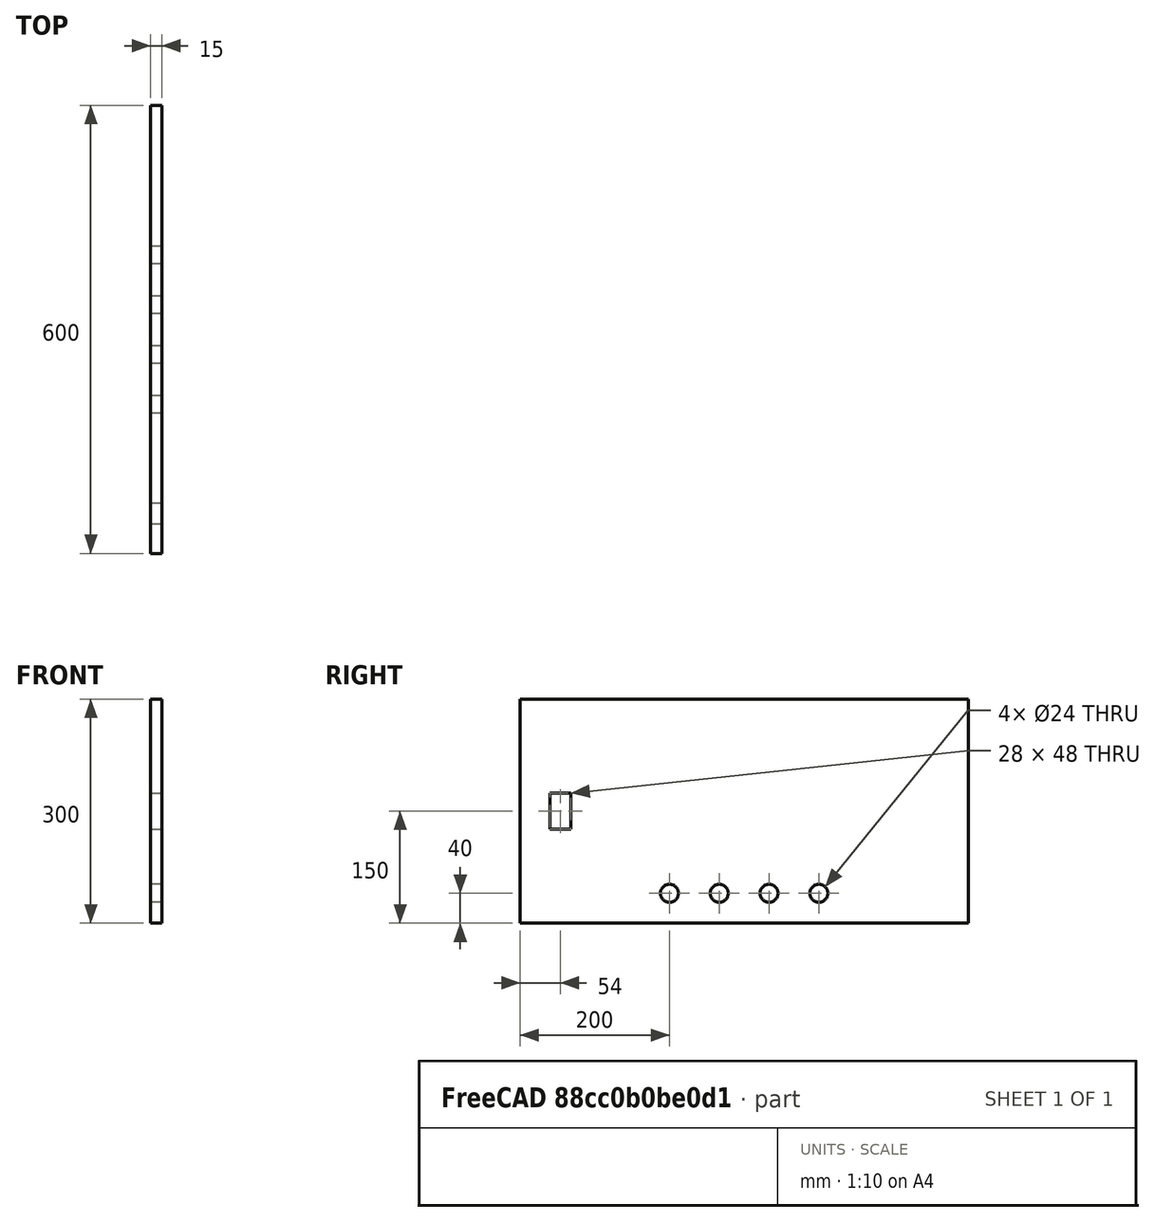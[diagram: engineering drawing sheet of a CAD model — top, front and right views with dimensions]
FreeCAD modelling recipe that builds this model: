
FCSTD DOCUMENT  (FreeCAD 1.0R39319 (Git))
Label: connector_panel
License: All rights reserved
LicenseURL: http://en.wikipedia.org/wiki/All_rights_reserved
objects: Sketcher::SketchObject×1, PartDesign::Pad×1, PartDesign::Body×1
note: 6 computed .brp shape members not serialized (recipe doc carries the construction recipe); baked Part::Feature solids carry a one-line shape summary decoded from their .brp

FEATURE [Sketcher::SketchObject] Sketch  label="connector_panel_sketch"
  ArcFitTolerance = 0
  AttachmentSupport = -> [YZ_Plane]
  FullyConstrained = true
  MakeInternals = false
  MapMode = 5
  Placement = pos=(0,0,0) rot=(0.57735,0.57735,0.57735;2.0944rad)
  sketch-geometry (21):
    g0: LineSegment StartX=0 StartY=0 StartZ=0 EndX=600 EndY=0 EndZ=0
    g1: LineSegment StartX=600 StartY=0 StartZ=0 EndX=600 EndY=300 EndZ=0
    g2: LineSegment StartX=600 StartY=300 StartZ=0 EndX=0 EndY=300 EndZ=0
    g3: LineSegment StartX=0 StartY=300 StartZ=0 EndX=0 EndY=0 EndZ=0
    g4: LineSegment StartX=40 StartY=174 StartZ=0 EndX=68 EndY=174 EndZ=0
    g5: LineSegment StartX=68 StartY=174 StartZ=0 EndX=68 EndY=126 EndZ=0
    g6: LineSegment StartX=68 StartY=126 StartZ=0 EndX=40 EndY=126 EndZ=0
    g7: LineSegment StartX=40 StartY=126 StartZ=0 EndX=40 EndY=174 EndZ=0
    g8: Circle CenterX=200 CenterY=40 CenterZ=0 NormalX=0 NormalY=0 NormalZ=1 AngleXU=0 Radius=12
    g9: Circle CenterX=266.667 CenterY=40 CenterZ=0 NormalX=0 NormalY=0 NormalZ=1 AngleXU=0 Radius=12
    g10: Circle CenterX=333.333 CenterY=40 CenterZ=0 NormalX=0 NormalY=0 NormalZ=1 AngleXU=0 Radius=12
    g11: Circle CenterX=400 CenterY=40 CenterZ=0 NormalX=0 NormalY=0 NormalZ=1 AngleXU=0 Radius=12
    g12: LineSegment [constr] StartX=40 StartY=126 StartZ=0 EndX=0 EndY=126 EndZ=0
    g13: LineSegment [constr] StartX=200 StartY=40 StartZ=0 EndX=266.667 EndY=40 EndZ=0
    g14: LineSegment [constr] StartX=333.333 StartY=40 StartZ=0 EndX=400 EndY=40 EndZ=0
    g15: LineSegment [constr] StartX=40 StartY=126 StartZ=0 EndX=40 EndY=0 EndZ=0
    g16: LineSegment [constr] StartX=40 StartY=174 StartZ=0 EndX=40 EndY=300 EndZ=0
    g17: LineSegment [constr] StartX=200 StartY=40 StartZ=0 EndX=200 EndY=0 EndZ=0
    g18: LineSegment [constr] StartX=266.667 StartY=40 StartZ=0 EndX=333.333 EndY=40 EndZ=0
    g19: LineSegment [constr] StartX=200 StartY=40 StartZ=0 EndX=0 EndY=40 EndZ=0
    g20: LineSegment [constr] StartX=400 StartY=40 StartZ=0 EndX=600 EndY=40 EndZ=0
  constraints (59):
    c: Coincident(g0,g1)
    c: Coincident(g1,g2)
    c: Coincident(g2,g3)
    c: Coincident(g3,g0)
    c: Horizontal(g0)
    c: Horizontal(g2)
    c: Vertical(g1)
    c: Vertical(g3)
    c: Coincident(g0,g-1)
    c: DistanceY(g3,g3) = 300
    c: DistanceX(g0,g0) = 600
    c: Coincident(g4,g5)
    c: Coincident(g5,g6)
    c: Coincident(g6,g7)
    c: Coincident(g7,g4)
    c: Horizontal(g4)
    c: Horizontal(g6)
    c: Vertical(g5)
    c: Vertical(g7)
    c: DistanceX(g4,g4) = 28
    c: DistanceY(g7,g7) = 48
    c: Radius(g8) = 12
    c: Radius(g9) = 12
    c: Radius(g10) = 12
    c: Radius(g11) = 12
    c: Coincident(g12,g6)
    c: PointOnObject(g12,g3)
    c: Horizontal(g12)
    c: Coincident(g13,g8)
    c: Coincident(g13,g9)
    c: Horizontal(g13)
    c: Coincident(g14,g10)
    c: Coincident(g14,g11)
    c: Horizontal(g14)
    c: Equal(g13,g14)
    c: Coincident(g15,g6)
    c: PointOnObject(g15,g0)
    c: Vertical(g15)
    c: Coincident(g16,g4)
    c: PointOnObject(g16,g2)
    c: Vertical(g16)
    c: Equal(g16,g15)
    c: DistanceX(g12,g12) = 40
    c: Coincident(g17,g8)
    c: PointOnObject(g17,g0)
    c: Vertical(g17)
    c: DistanceX(g-1,g17) = 200
    c: Coincident(g18,g9)
    c: Coincident(g18,g10)
    c: Horizontal(g18)
    c: Equal(g18,g14)
    c: DistanceY(g17,g17) = 40
    c: Coincident(g19,g8)
    c: PointOnObject(g19,g3)
    c: Horizontal(g19)
    c: Coincident(g20,g11)
    c: PointOnObject(g20,g1)
    c: Horizontal(g20)
    c: Equal(g19,g20)
FEATURE [PartDesign::Pad] Pad  label="connector_panel_pad"
  AllowMultiFace = false
  Direction = (1,-1.129e-13,1.129e-13)
  Length = 15
  Length2 = 100
  Placement = pos=(0,0,0) rot=(0.57735,0.57735,0.57735;2.0944rad)
  Profile = -> Sketch
  ReferenceAxis = -> Sketch [N_Axis]
  Suppressed = false
  Type = 0
FEATURE [PartDesign::Body] Body  label="connector_panel_body"
  AllowCompound = false
  Group = -> [Sketch,Pad]
  Origin = -> Origin
  Tip = -> Pad
